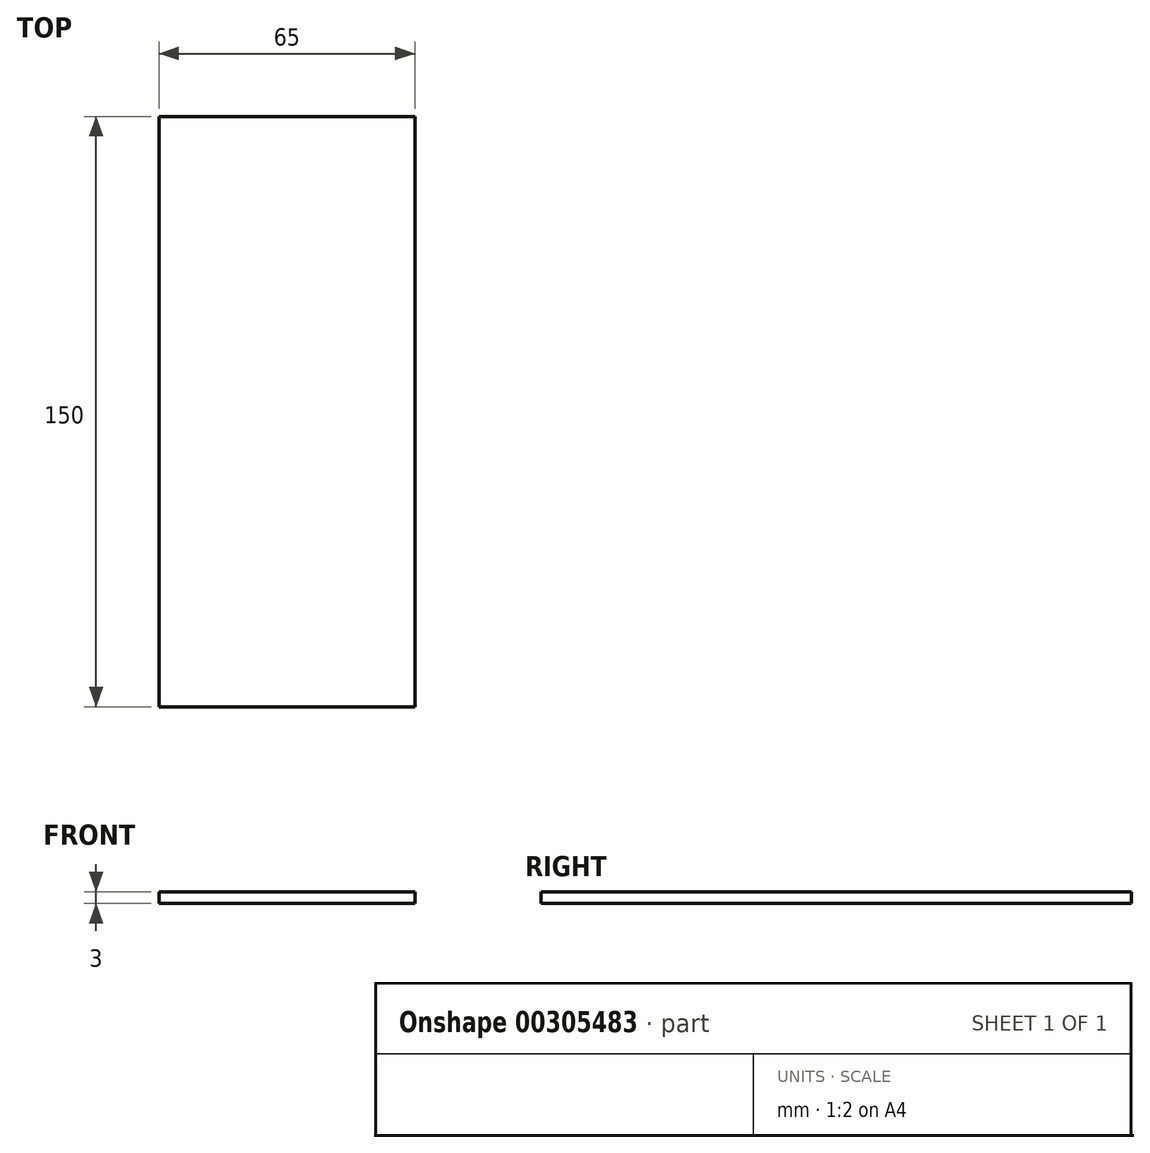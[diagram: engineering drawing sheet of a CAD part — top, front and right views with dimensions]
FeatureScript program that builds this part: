
annotation { "Feature Type Name" : "Feature", "Feature Type Description" : "" }
export const myFeature = defineFeature(function(context is Context, id is Id, definition is map)
    precondition{}
    {
        {
            var Q0;
            Q0=qCreatedBy(makeId("Top.planeOp"),FACE);
            var sketch = newSketch(context, id + "F0", { "sketchPlane" : qUnion([Q0])});
            skLineSegment(sketch, "E0.bottom", {"start": v(-32.5, 75) * mm, "end": v(32.5, 75) * mm});
            skLineSegment(sketch, "E0.top", {"start": v(-32.5, -75) * mm, "end": v(32.5, -75) * mm});
            skLineSegment(sketch, "E0.left", {"start": v(-32.5, 75) * mm, "end": v(-32.5, -75) * mm});
            skLineSegment(sketch, "E0.right", {"start": v(32.5, 75) * mm, "end": v(32.5, -75) * mm});
            skPoint(sketch, "E0.middle", {"position": v(0, 0) * mm});
            skSolve(sketch);
        }
        {
            var Q0;
            Q0=makeQuery(id+"F0.imprint","IMPRINT",FACE,{"disambiguationData":[TD([[makeQuery(id+"F0.imprint","IMPRINT",EDGE,{"derivedFrom":sQuery(id+"F0.wireOp",EDGE,"E0.bottom")}),-1.0]])]});
            extrude(context, id + "F1", {"entities" : qUnion([Q0]), "depth" : 3 * mm});
        }
    });
